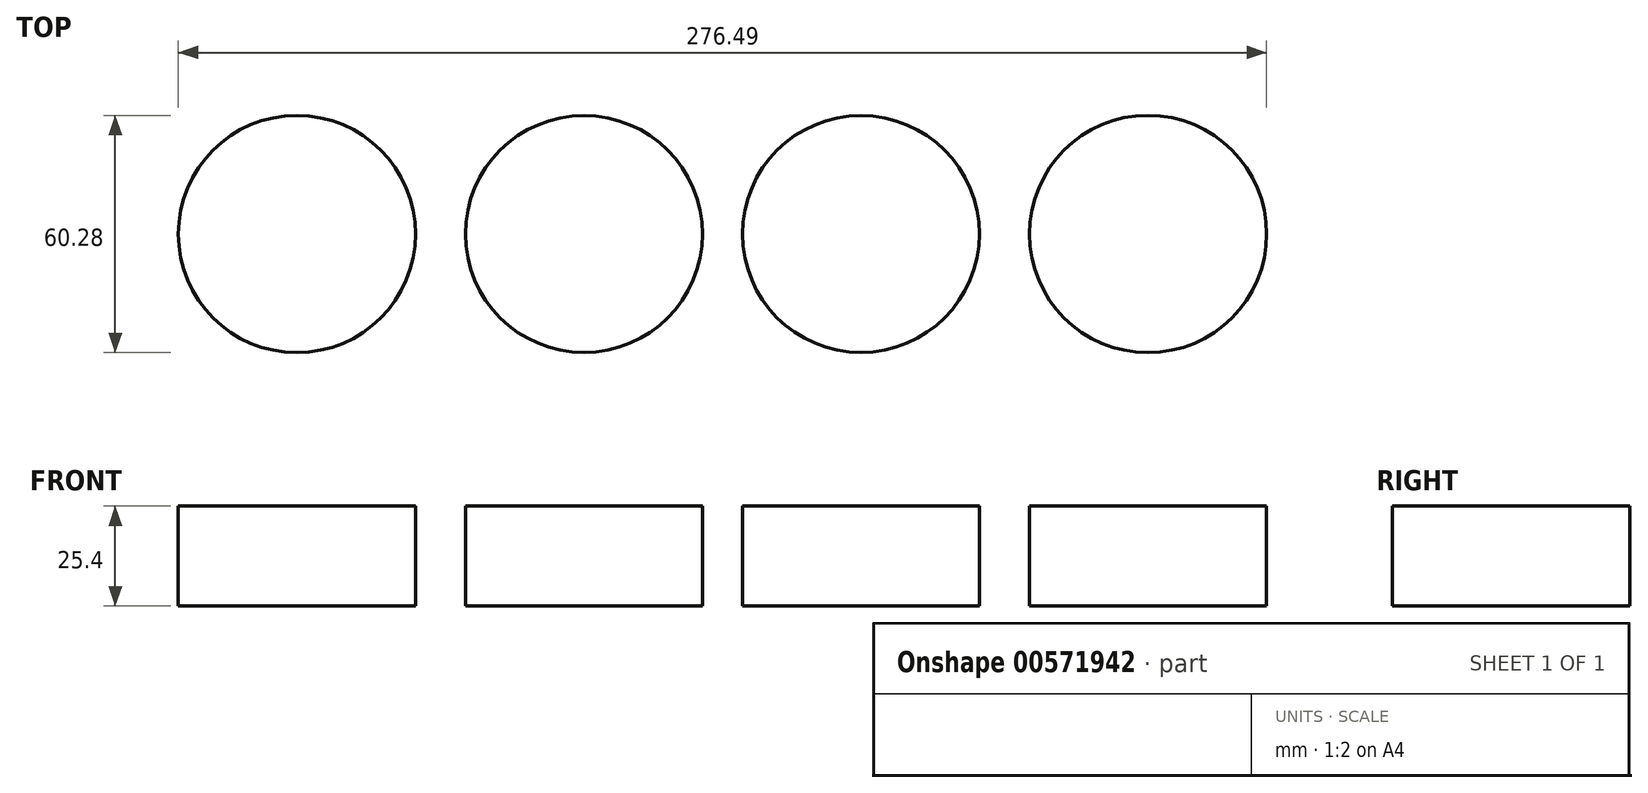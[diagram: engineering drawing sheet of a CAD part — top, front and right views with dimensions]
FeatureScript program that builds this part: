
annotation { "Feature Type Name" : "Feature", "Feature Type Description" : "" }
export const myFeature = defineFeature(function(context is Context, id is Id, definition is map)
    precondition{}
    {
        {
            var Q0;
            Q0=qCreatedBy(makeId("Top.planeOp"),FACE);
            var sketch = newSketch(context, id + "F0", { "sketchPlane" : qUnion([Q0])});
            skCircle(sketch, "E0", {"center": v(0, 0) * mm, "radius": 30.1 * mm});
            skCircle(sketch, "E1", {"center": v(-70.36, 0) * mm, "radius": 30.11 * mm});
            skCircle(sketch, "E2", {"center": v(-143.3, 0) * mm, "radius": 30.12 * mm});
            skCircle(sketch, "E3", {"center": v(72.94, 0) * mm, "radius": 30.14 * mm});
            skSolve(sketch);
        }
        {
            var Q0;
            Q0 = qSketchRegion(id + "F0", true);
            extrude(context, id + "F1", {"entities" : qUnion([Q0]), "depth" : 25.4 * mm, "offsetDistance" : 25.4 * mm});
        }
    });
